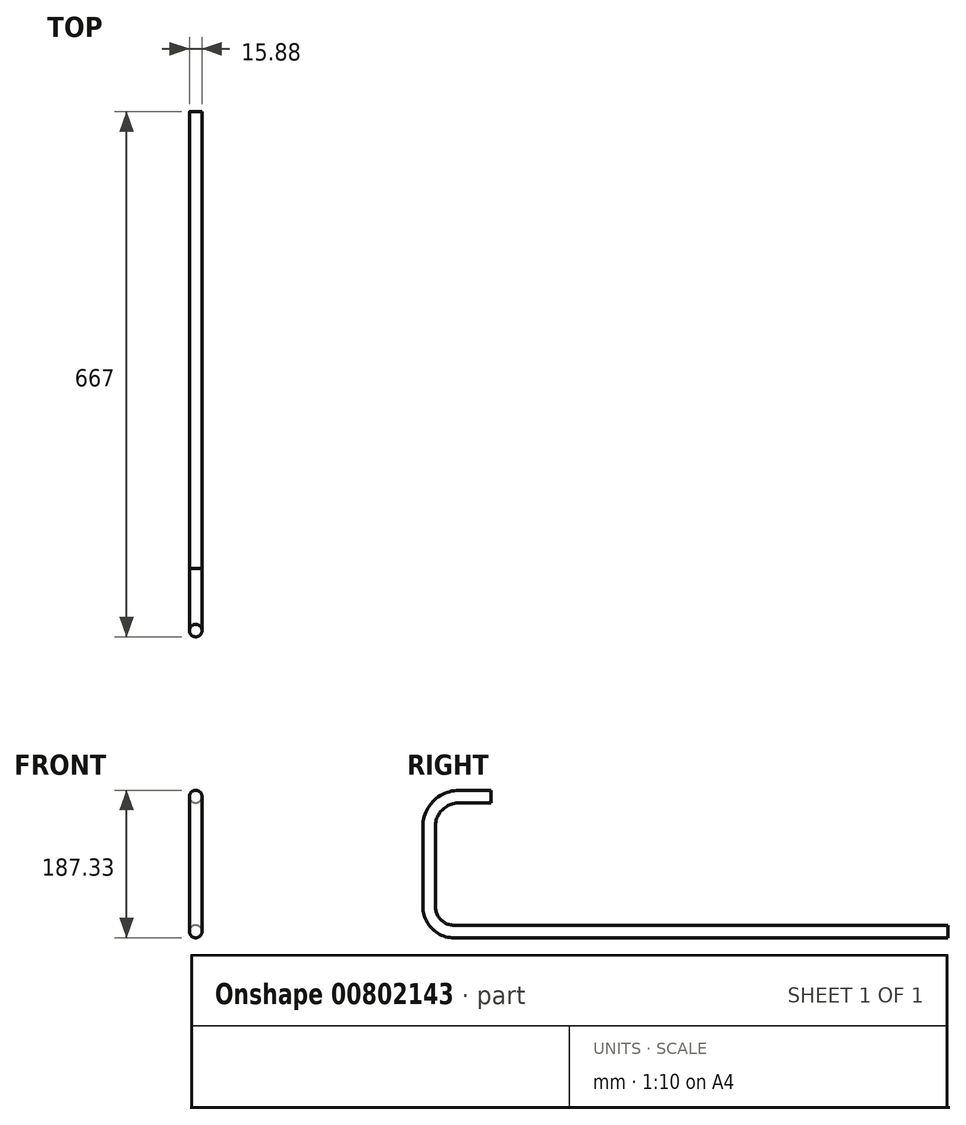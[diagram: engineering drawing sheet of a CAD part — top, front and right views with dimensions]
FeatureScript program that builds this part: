
annotation { "Feature Type Name" : "Feature", "Feature Type Description" : "" }
export const myFeature = defineFeature(function(context is Context, id is Id, definition is map)
    precondition{}
    {
        {
            var Q0;
            Q0=qCreatedBy(makeId("Front.planeOp"),FACE);
            var sketch = newSketch(context, id + "F0", { "sketchPlane" : qUnion([Q0])});
            skCircle(sketch, "E0", {"center": v(0, 0) * mm, "radius": 7.94 * mm});
            skSolve(sketch);
        }
        {
            var Q0;
            Q0=qCreatedBy(makeId("Right.planeOp"),FACE);
            var sketch = newSketch(context, id + "F1", { "sketchPlane" : qUnion([Q0])});
            skLineSegment(sketch, "E1", {"start": v(0, 0) * mm, "end": v(-40.73, 0) * mm});
            skLineSegment(sketch, "E2", {"start": v(-78.83, -38.1) * mm, "end": v(-78.83, -139.7) * mm});
            skLineSegment(sketch, "E3", {"start": v(-47.08, -171.45) * mm, "end": v(580.24, -171.45) * mm});
            skPoint(sketch, "E4.visualSharp", {"position": v(-78.83, 0) * mm});
            skArc(sketch, "E4.filletArc", {"start": v(-40.73, 0) * mm, "mid": v(-67.67, -11.16) * mm, "end": v(-78.83, -38.1) * mm});
            skPoint(sketch, "E5.visualSharp", {"position": v(-78.83, -171.45) * mm});
            skArc(sketch, "E5.filletArc", {"start": v(-78.83, -139.7) * mm, "mid": v(-69.53, -162.15) * mm, "end": v(-47.08, -171.45) * mm});
            skSolve(sketch);
        }
        {
            var Q0;
            Q0=qSketchRegion(id+"F0",true);
            var Q1;
            Q1=qConstructionFilter(qBodyType(qCreatedBy(id+"F1",EDGE),BodyType.WIRE),ConstructionObject.NO);
            sweep(context, id + "F2", {"profiles" : qUnion([Q0]), "path" : qUnion([Q1])});
        }
    });
